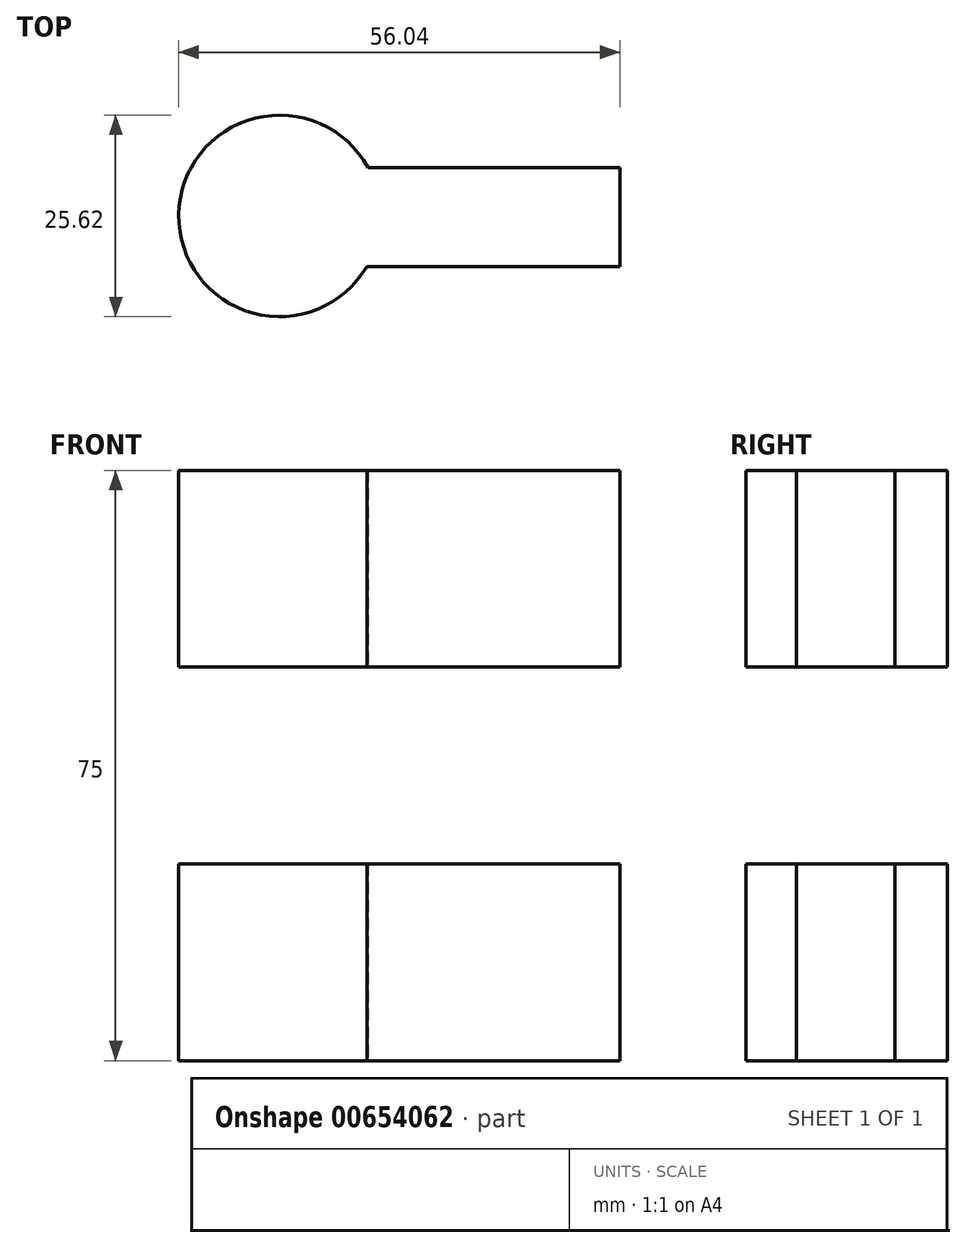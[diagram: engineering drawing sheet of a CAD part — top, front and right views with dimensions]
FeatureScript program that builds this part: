
annotation { "Feature Type Name" : "Feature", "Feature Type Description" : "" }
export const myFeature = defineFeature(function(context is Context, id is Id, definition is map)
    precondition{}
    {
        {
            var Q0;
            Q0=qCreatedBy(makeId("Top.planeOp"),FACE);
            var sketch = newSketch(context, id + "F0", { "sketchPlane" : qUnion([Q0])});
            skCircle(sketch, "E0", {"center": v(0, 0) * mm, "radius": 12.8 * mm});
            skLineSegment(sketch, "E1.bottom", {"start": v(3.95, -6.4) * mm, "end": v(43.23, -6.4) * mm});
            skLineSegment(sketch, "E1.top", {"start": v(3.95, 6.14) * mm, "end": v(43.23, 6.14) * mm});
            skLineSegment(sketch, "E1.left", {"start": v(3.95, -6.4) * mm, "end": v(3.95, 6.14) * mm});
            skLineSegment(sketch, "E1.right", {"start": v(43.23, -6.4) * mm, "end": v(43.23, 6.14) * mm});
            skSolve(sketch);
        }
        {
            var Q0;
            {var subQ5=sQuery(id+"F0.wireOp",EDGE,"E1.left");Q0=makeQuery(id+"F0.imprint","IMPRINT",FACE,{"disambiguationData":[TD([[makeQuery(id+"F0.imprint","IMPRINT",EDGE,{"derivedFrom":subQ5}),-1.0]])]});}
            var Q1;
            {var subQ5=sQuery(id+"F0.wireOp",EDGE,"E1.right");Q1=makeQuery(id+"F0.imprint","IMPRINT",FACE,{"disambiguationData":[TD([[makeQuery(id+"F0.imprint","IMPRINT",EDGE,{"derivedFrom":subQ5}),1.0]])]});}
            var Q2;
            {var subQ5=sQuery(id+"F0.wireOp",EDGE,"E1.left");Q2=makeQuery(id+"F0.imprint","IMPRINT",FACE,{"disambiguationData":[TD([[makeQuery(id+"F0.imprint","IMPRINT",EDGE,{"derivedFrom":subQ5}),1.0]])]});}
            extrude(context, id + "F1", {"entities" : qUnion([Q0, Q1, Q2]), "depth" : 25 * mm, "offsetDistance" : 25 * mm});
        }
        {
            var Q0;
            Q0=makeQuery(id+"F1.opExtrude","CAP_FACE",FACE,{"disambiguationData":[OSD([sQuery(id+"F0.wireOp",EDGE,"E0"),sQuery(id+"F0.wireOp",EDGE,"E1.bottom"),sQuery(id+"F0.wireOp",EDGE,"E1.top"),sQuery(id+"F0.wireOp",EDGE,"E1.right")])],"isStart":false});
            cPlane(context, id + "F2", {"entities" : qUnion([Q0]), "cplaneType" : CPlaneType.OFFSET, "offset" : 25 * mm, "width" : 150 * mm, "height" : 150 * mm});
        }
        {
            var Q0;
            Q0=qCreatedBy(id+"F2.planeOp",FACE);
            var sketch = newSketch(context, id + "F3", { "sketchPlane" : qUnion([Q0])});
            skLineSegment(sketch, "E2.bottom", {"start": v(-16.25, 3.02) * mm, "end": v(23.02, 3.02) * mm});
            skArc(sketch, "E3.0.0", {"start": v(11.24, 6.14) * mm, "mid": v(-12.8, 0.16) * mm, "end": v(11.09, -6.4) * mm});
            skLineSegment(sketch, "E3.0.1", {"start": v(11.09, -6.4) * mm, "end": v(43.23, -6.4) * mm});
            skLineSegment(sketch, "E3.0.2", {"start": v(43.23, -6.4) * mm, "end": v(43.23, 6.14) * mm});
            skLineSegment(sketch, "E3.0.3", {"start": v(43.23, 6.14) * mm, "end": v(11.24, 6.14) * mm});
            skSolve(sketch);
        }
        {
            var Q0;
            {var subQ2=sQuery(id+"F3.wireOp",EDGE,"E3.0.1");Q0=makeQuery(id+"F3.imprint","IMPRINT",FACE,{"disambiguationData":[TD([[makeQuery(id+"F3.imprint","IMPRINT",EDGE,{"derivedFrom":subQ2}),1.0]])]});}
            extrude(context, id + "F4", {"entities" : qUnion([Q0]), "depth" : 25 * mm, "offsetDistance" : 25 * mm});
        }
    });
